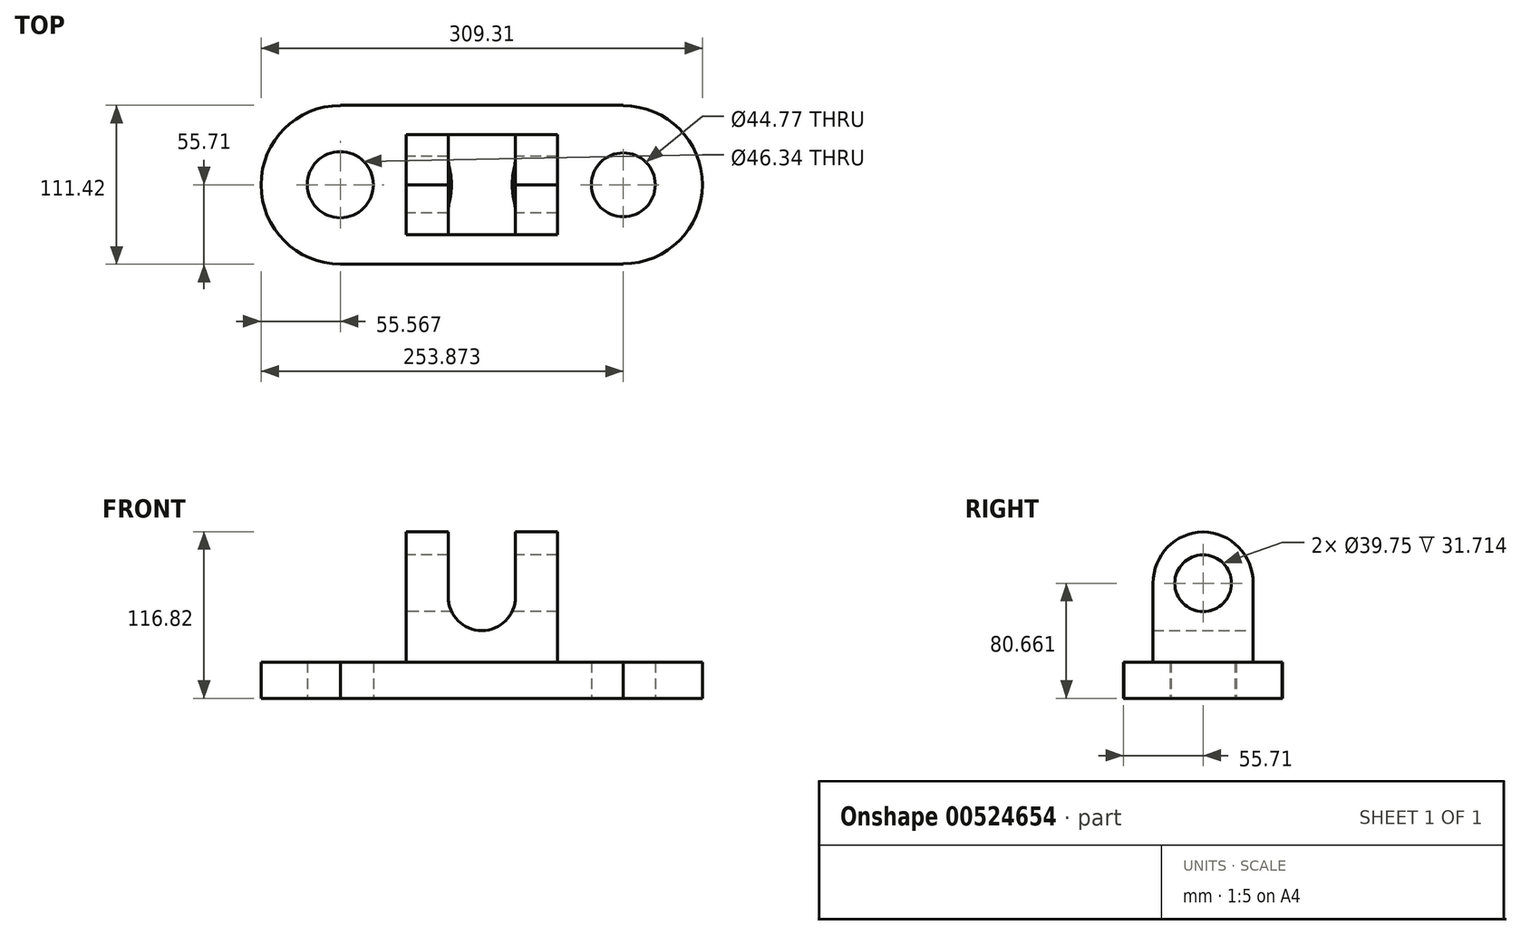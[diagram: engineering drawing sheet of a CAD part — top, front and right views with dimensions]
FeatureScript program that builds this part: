
annotation { "Feature Type Name" : "Feature", "Feature Type Description" : "" }
export const myFeature = defineFeature(function(context is Context, id is Id, definition is map)
    precondition{}
    {
        {
            var Q0;
            Q0=qCreatedBy(makeId("Top.planeOp"),FACE);
            var sketch = newSketch(context, id + "F0", { "sketchPlane" : qUnion([Q0])});
            skLineSegment(sketch, "E0.bottom", {"start": v(99.15, -55.71) * mm, "end": v(-99.15, -55.71) * mm});
            skLineSegment(sketch, "E0.top", {"start": v(99.15, 55.71) * mm, "end": v(-99.15, 55.71) * mm});
            skLineSegment(sketch, "E0.left", {"start": v(99.15, -55.71) * mm, "end": v(99.15, 55.71) * mm});
            skLineSegment(sketch, "E0.right", {"start": v(-99.15, -55.71) * mm, "end": v(-99.15, 55.71) * mm});
            skPoint(sketch, "E0.middle", {"position": v(0, 0) * mm});
            skCircle(sketch, "E1", {"center": v(-99.15, 0) * mm, "radius": 55.57 * mm});
            skCircle(sketch, "E2", {"center": v(99.15, 0) * mm, "radius": 55.43 * mm});
            skCircle(sketch, "E3", {"center": v(-99.15, 0) * mm, "radius": 23.17 * mm});
            skCircle(sketch, "E4", {"center": v(99.15, 0) * mm, "radius": 22.39 * mm});
            skSolve(sketch);
        }
        {
            var Q0;
            {var subQ1=sQuery(id+"F0.wireOp",EDGE,"E0.bottom");Q0=makeQuery(id+"F0.imprint","IMPRINT",FACE,{"disambiguationData":[TD([[makeQuery(id+"F0.imprint","IMPRINT",EDGE,{"derivedFrom":subQ1}),-1.0]])]});}
            var Q1;
            {var subQ0=sQuery(id+"F0.wireOp",EDGE,"E2");var subQ1=sQuery(id+"F0.wireOp",EDGE,"E0.left");var subQ2=makeQuery(id+"F0.imprint","INTERSECT",VERTEX,{"disambiguationData":[OD(0.0)],"derivedFrom":[subQ1,subQ0]});Q1=makeQuery(id+"F0.imprint","IMPRINT",FACE,{"disambiguationData":[TD([[makeQuery(id+"F0.imprint","IMPRINT",EDGE,{"disambiguationData":[TD([[subQ2,-1.0]])],"derivedFrom":subQ1}),-1.0]])]});}
            var Q2;
            {var subQ0=sQuery(id+"F0.wireOp",EDGE,"E1");var subQ1=sQuery(id+"F0.wireOp",EDGE,"E0.right");var subQ2=makeQuery(id+"F0.imprint","INTERSECT",VERTEX,{"disambiguationData":[OD(0.0)],"derivedFrom":[subQ1,subQ0]});Q2=makeQuery(id+"F0.imprint","IMPRINT",FACE,{"disambiguationData":[TD([[makeQuery(id+"F0.imprint","IMPRINT",EDGE,{"disambiguationData":[TD([[subQ2,-1.0]])],"derivedFrom":subQ1}),1.0]])]});}
            var Q3;
            {var subQ0=sQuery(id+"F0.wireOp",EDGE,"E2");var subQ1=sQuery(id+"F0.wireOp",EDGE,"E0.left");var subQ2=makeQuery(id+"F0.imprint","INTERSECT",VERTEX,{"disambiguationData":[OD(0.0)],"derivedFrom":[subQ1,subQ0]});Q3=makeQuery(id+"F0.imprint","IMPRINT",FACE,{"disambiguationData":[TD([[makeQuery(id+"F0.imprint","IMPRINT",EDGE,{"disambiguationData":[TD([[subQ2,-1.0]])],"derivedFrom":subQ1}),1.0]])]});}
            var Q4;
            {var subQ0=sQuery(id+"F0.wireOp",EDGE,"E1");var subQ1=sQuery(id+"F0.wireOp",EDGE,"E0.right");var subQ2=makeQuery(id+"F0.imprint","INTERSECT",VERTEX,{"disambiguationData":[OD(0.0)],"derivedFrom":[subQ1,subQ0]});Q4=makeQuery(id+"F0.imprint","IMPRINT",FACE,{"disambiguationData":[TD([[makeQuery(id+"F0.imprint","IMPRINT",EDGE,{"disambiguationData":[TD([[subQ2,-1.0]])],"derivedFrom":subQ1}),-1.0]])]});}
            extrude(context, id + "F1", {"entities" : qUnion([Q0, Q1, Q2, Q3, Q4]), "depth" : 25.4 * mm, "offsetDistance" : 25.4 * mm});
        }
        {
            var Q0;
            Q0=makeQuery(id+"F1.opExtrude","CAP_FACE",FACE,{"disambiguationData":[OSD([sQuery(id+"F0.wireOp",EDGE,"E0.bottom"),sQuery(id+"F0.wireOp",EDGE,"E0.top"),sQuery(id+"F0.wireOp",EDGE,"E0.left"),sQuery(id+"F0.wireOp",EDGE,"E0.right"),sQuery(id+"F0.wireOp",EDGE,"E1"),sQuery(id+"F0.wireOp",EDGE,"E2"),sQuery(id+"F0.wireOp",EDGE,"E3"),sQuery(id+"F0.wireOp",EDGE,"E4")])],"isStart":false});
            var sketch = newSketch(context, id + "F2", { "sketchPlane" : qUnion([Q0])});
            skLineSegment(sketch, "E5.bottom", {"start": v(52.94, -35.1) * mm, "end": v(-52.94, -35.1) * mm});
            skLineSegment(sketch, "E5.top", {"start": v(52.94, 35.1) * mm, "end": v(-52.94, 35.1) * mm});
            skLineSegment(sketch, "E5.left", {"start": v(52.94, -35.1) * mm, "end": v(52.94, 35.1) * mm});
            skLineSegment(sketch, "E5.right", {"start": v(-52.94, -35.1) * mm, "end": v(-52.94, 35.1) * mm});
            skPoint(sketch, "E5.middle", {"position": v(0, 0) * mm});
            skSolve(sketch);
        }
        {
            var Q0;
            Q0=makeQuery(id+"F2.imprint","IMPRINT",FACE,{"disambiguationData":[TD([[makeQuery(id+"F2.imprint","IMPRINT",EDGE,{"derivedFrom":sQuery(id+"F2.wireOp",EDGE,"E5.bottom")}),-1.0]])]});
            extrude(context, id + "F3", {"entities" : qUnion([Q0]), "operationType" : NewBodyOperationType.ADD, "depth" : 55.88 * mm, "offsetDistance" : 25.4 * mm});
        }
        {
            var Q0;
            Q0=makeQuery(id+"F3.opExtrude","CAP_FACE",FACE,{"disambiguationData":[OSD([sQuery(id+"F2.wireOp",EDGE,"E5.bottom"),sQuery(id+"F2.wireOp",EDGE,"E5.top"),sQuery(id+"F2.wireOp",EDGE,"E5.left"),sQuery(id+"F2.wireOp",EDGE,"E5.right")])],"isStart":false});
            var sketch = newSketch(context, id + "F4", { "sketchPlane" : qUnion([Q0])});
            skLineSegment(sketch, "E6.bottom", {"start": v(23.5, -35.1) * mm, "end": v(-23.5, -35.1) * mm});
            skLineSegment(sketch, "E6.top", {"start": v(23.5, 35.1) * mm, "end": v(-23.5, 35.1) * mm});
            skLineSegment(sketch, "E6.left", {"start": v(23.5, -35.1) * mm, "end": v(23.5, 35.1) * mm});
            skLineSegment(sketch, "E6.right", {"start": v(-23.5, -35.1) * mm, "end": v(-23.5, 35.1) * mm});
            skPoint(sketch, "E6.middle", {"position": v(0, 0) * mm});
            skSolve(sketch);
        }
        {
            var Q0;
            Q0=makeQuery(id+"F4.imprint","IMPRINT",FACE,{"disambiguationData":[TD([[makeQuery(id+"F4.imprint","IMPRINT",EDGE,{"derivedFrom":sQuery(id+"F4.wireOp",EDGE,"E6.bottom")}),-1.0]])]});
            extrude(context, id + "F5", {"entities" : qUnion([Q0]), "operationType" : NewBodyOperationType.REMOVE, "oppositeDirection" : true, "depth" : 33.78 * mm, "offsetDistance" : 25.4 * mm});
        }
        {
            var Q0;
            Q0=makeQuery(id+"F5.boolean.opBoolean","COPY",EDGE,{"derivedFrom":makeQuery(id+"F5.opExtrude","CAP_EDGE",EDGE,{"disambiguationData":[OSD([sQuery(id+"F4.wireOp",EDGE,"E6.right")])],"isStart":false})});
            var Q1;
            Q1=makeQuery(id+"F5.boolean.opBoolean","COPY",EDGE,{"derivedFrom":makeQuery(id+"F5.opExtrude","CAP_EDGE",EDGE,{"disambiguationData":[OSD([sQuery(id+"F4.wireOp",EDGE,"E6.left")])],"isStart":false})});
            fillet(context, id + "F6", {"entities" : qUnion([Q0, Q1]), "radius" : 23.3 * mm, "tangentPropagation" : true, "allowEdgeOverflow" : false});
        }
        {
            var Q0;
            {var subQ0=sQuery(id+"F2.wireOp",EDGE,"E5.bottom");var subQ1=sQuery(id+"F2.wireOp",EDGE,"E5.right");var subQ2=sQuery(id+"F2.wireOp",EDGE,"E5.top");Q0=makeQuery(id+"F5.boolean.opBoolean","SPLIT",FACE,{"disambiguationData":[TD([makeQuery(id+"F3.opExtrude","SWEPT_FACE",FACE,{"disambiguationData":[OSD([subQ1])]})])],"derivedFrom":makeQuery(id+"F3.opExtrude","CAP_FACE",FACE,{"disambiguationData":[OSD([subQ0,subQ2,sQuery(id+"F2.wireOp",EDGE,"E5.left"),subQ1])],"isStart":false})});}
            var Q1;
            {var subQ0=sQuery(id+"F2.wireOp",EDGE,"E5.bottom");var subQ1=sQuery(id+"F2.wireOp",EDGE,"E5.top");var subQ2=sQuery(id+"F2.wireOp",EDGE,"E5.left");Q1=makeQuery(id+"F5.boolean.opBoolean","SPLIT",FACE,{"disambiguationData":[TD([makeQuery(id+"F3.opExtrude","SWEPT_FACE",FACE,{"disambiguationData":[OSD([subQ2])]})])],"derivedFrom":makeQuery(id+"F3.opExtrude","CAP_FACE",FACE,{"disambiguationData":[OSD([subQ0,subQ1,subQ2,sQuery(id+"F2.wireOp",EDGE,"E5.right")])],"isStart":false})});}
            extrude(context, id + "F7", {"entities" : qUnion([Q0, Q1]), "operationType" : NewBodyOperationType.ADD, "depth" : 35.56 * mm, "offsetDistance" : 25.4 * mm});
        }
        {
            var Q0;
            {var subQ0=sQuery(id+"F2.wireOp",EDGE,"E5.bottom");var subQ1=sQuery(id+"F2.wireOp",EDGE,"E5.right");Q0=makeQuery(id+"F7.opExtrude","CAP_EDGE",EDGE,{"disambiguationData":[OSD([subQ0]),TDD([makeQuery(id+"F5.boolean.opBoolean","SPLIT",EDGE,{"disambiguationData":[TD([makeQuery(id+"F3.opExtrude","SWEPT_FACE",FACE,{"disambiguationData":[OSD([subQ1])]})])],"derivedFrom":makeQuery(id+"F3.opExtrude","CAP_EDGE",EDGE,{"disambiguationData":[OSD([subQ0])],"isStart":false})})])],"isStart":false});}
            var Q1;
            {var subQ0=sQuery(id+"F2.wireOp",EDGE,"E5.right");var subQ1=sQuery(id+"F2.wireOp",EDGE,"E5.top");Q1=makeQuery(id+"F7.opExtrude","CAP_EDGE",EDGE,{"disambiguationData":[OSD([subQ1]),TDD([makeQuery(id+"F5.boolean.opBoolean","SPLIT",EDGE,{"disambiguationData":[TD([makeQuery(id+"F3.opExtrude","SWEPT_FACE",FACE,{"disambiguationData":[OSD([subQ0])]})])],"derivedFrom":makeQuery(id+"F3.opExtrude","CAP_EDGE",EDGE,{"disambiguationData":[OSD([subQ1])],"isStart":false})})])],"isStart":false});}
            var Q2;
            {var subQ0=sQuery(id+"F2.wireOp",EDGE,"E5.bottom");var subQ1=sQuery(id+"F2.wireOp",EDGE,"E5.left");Q2=makeQuery(id+"F7.opExtrude","CAP_EDGE",EDGE,{"disambiguationData":[OSD([subQ0]),TDD([makeQuery(id+"F5.boolean.opBoolean","SPLIT",EDGE,{"disambiguationData":[TD([makeQuery(id+"F3.opExtrude","SWEPT_FACE",FACE,{"disambiguationData":[OSD([subQ1])]})])],"derivedFrom":makeQuery(id+"F3.opExtrude","CAP_EDGE",EDGE,{"disambiguationData":[OSD([subQ0])],"isStart":false})})])],"isStart":false});}
            var Q3;
            {var subQ0=sQuery(id+"F2.wireOp",EDGE,"E5.left");var subQ1=sQuery(id+"F2.wireOp",EDGE,"E5.top");Q3=makeQuery(id+"F7.opExtrude","CAP_EDGE",EDGE,{"disambiguationData":[OSD([subQ1]),TDD([makeQuery(id+"F5.boolean.opBoolean","SPLIT",EDGE,{"disambiguationData":[TD([makeQuery(id+"F3.opExtrude","SWEPT_FACE",FACE,{"disambiguationData":[OSD([subQ0])]})])],"derivedFrom":makeQuery(id+"F3.opExtrude","CAP_EDGE",EDGE,{"disambiguationData":[OSD([subQ1])],"isStart":false})})])],"isStart":false});}
            fillet(context, id + "F8", {"entities" : qUnion([Q0, Q1, Q2, Q3]), "radius" : 36.18 * mm, "tangentPropagation" : true, "allowEdgeOverflow" : false});
        }
        {
            var Q0;
            {var subQ0=sQuery(id+"F2.wireOp",EDGE,"E5.right");Q0=makeQuery(id+"F7.boolean.opBoolean","MERGE",FACE,{"derivedFrom":[makeQuery(id+"F3.opExtrude","SWEPT_FACE",FACE,{"disambiguationData":[OSD([subQ0])]}),makeQuery(id+"F7.opExtrude","SWEPT_FACE",FACE,{"disambiguationData":[OSD([subQ0])]})]});}
            var sketch = newSketch(context, id + "F9", { "sketchPlane" : qUnion([Q0])});
            skCircle(sketch, "E7", {"center": v(0, 80.66) * mm, "radius": 19.87 * mm});
            skPoint(sketch, "E7.centerSnap0", {"position": v(0, 25.4) * mm});
            skSolve(sketch);
        }
        {
            var Q0;
            Q0=makeQuery(id+"F9.imprint","IMPRINT",FACE,{"disambiguationData":[TD([[makeQuery(id+"F9.imprint","IMPRINT",EDGE,{"derivedFrom":sQuery(id+"F9.wireOp",EDGE,"E7")}),1.0]])]});
            extrude(context, id + "F10", {"entities" : qUnion([Q0]), "operationType" : NewBodyOperationType.REMOVE, "endBound" : BoundingType.THROUGH_ALL, "oppositeDirection" : true, "depth" : 25.4 * mm, "offsetDistance" : 25.4 * mm});
        }
    });
